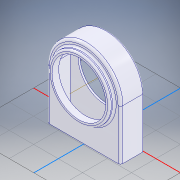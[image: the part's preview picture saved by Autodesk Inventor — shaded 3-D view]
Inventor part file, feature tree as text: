
AUTODESK INVENTOR PART (.ipt)
format: ipt  version: 2022 (Build 260153000, 153)  size: 220,160 bytes
history: native  units: mm
features: sketch x6, extrude x5, other x3, fillet x3, projected_geometry x2, revolve x1
ambient origin geometry x8: Origin, YZ Plane, XZ Plane, XY Plane, X Axis, Y Axis, Z Axis, Center Point
bodies: Body1 (feature_tree)
feature tree (20):
  other  "Твердое тело1"
  extrude  "Выдавливание1"  Depth=60.0mm
  extrude  "Выдавливание2"  Depth=71.0mm
  extrude  "Выдавливание3"  Depth=19.0mm TaperAngle=0.0deg
  fillet  "Сопряжение1"  Radius=44.0mm
  extrude  "Выдавливание4"  Depth=60.0mm
  sketch  "Эскиз5"
  other  "РабПлоскость1"
  extrude  "Выдавливание5"  Depth=8.0mm
  revolve  "Вращение1"
  fillet  "Сопряжение2"  [1 undecoded]
  fillet  "Сопряжение3"  Radius=50.0mm
  sketch  "Эскиз1"
  sketch  "Эскиз2"
  sketch  "Эскиз3"
  sketch  "Эскиз4"
  projected_geometry  "Спроецированная петля1"
  other  "РабОсь1"
  sketch  "Эскиз6"
  projected_geometry  "Спроецированная петля2"
note: 1 required parameter value undecoded (feature->parameter linkage not recoverable at this tier; creation-order binding heuristic only, values carry confidence <= 0.55)
